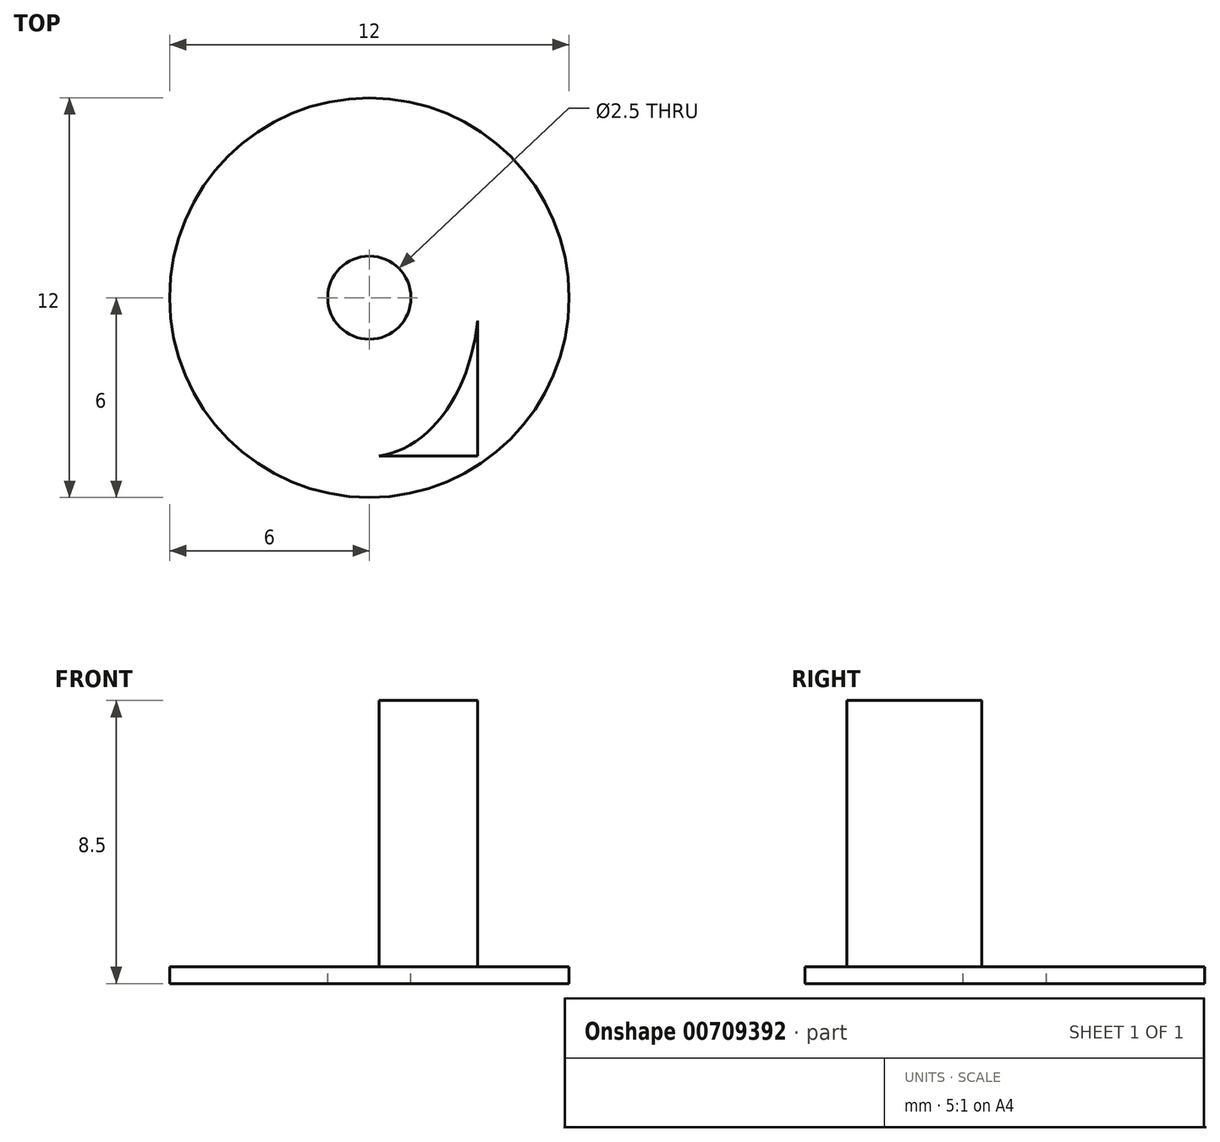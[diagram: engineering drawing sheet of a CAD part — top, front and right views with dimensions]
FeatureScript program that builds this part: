
annotation { "Feature Type Name" : "Feature", "Feature Type Description" : "" }
export const myFeature = defineFeature(function(context is Context, id is Id, definition is map)
    precondition{}
    {
        {
            var Q0;
            Q0=qCreatedBy(makeId("Top.planeOp"),FACE);
            var sketch = newSketch(context, id + "F0", { "sketchPlane" : qUnion([Q0])});
            skLineSegment(sketch, "E0.bottom", {"start": v(0, 0) * mm, "end": v(6.5, 0) * mm});
            skLineSegment(sketch, "E0.top", {"start": v(0, 9.5) * mm, "end": v(6.5, 9.5) * mm});
            skLineSegment(sketch, "E0.left", {"start": v(0, 0) * mm, "end": v(0, 9.5) * mm});
            skLineSegment(sketch, "E0.right", {"start": v(6.5, 0) * mm, "end": v(6.5, 9.5) * mm});
            skEllipse(sketch, "E1", {"center": v(3.25, 4.75) * mm, "majorRadius": 4.77 * mm, "minorRadius": 3.29 * mm, "majorAxis": v(0, -1)});
            skPoint(sketch, "E1.centerSnap0", {"position": v(0, 4.75) * mm});
            skPoint(sketch, "E1.centerSnap1", {"position": v(3.25, 9.5) * mm});
            skSolve(sketch);
        }
        {
            var Q0;
            {var subQ0=sQuery(id+"F0.wireOp",EDGE,"E1");var subQ7=sQuery(id+"F0.wireOp",EDGE,"E0.bottom");var subQ8=makeQuery(id+"F0.imprint","INTERSECT",VERTEX,{"disambiguationData":[OD(0.0)],"derivedFrom":[subQ7,subQ0]});Q0=makeQuery(id+"F0.imprint","IMPRINT",FACE,{"disambiguationData":[TD([[makeQuery(id+"F0.imprint","IMPRINT",EDGE,{"disambiguationData":[TD([[subQ8,-1.0]])],"derivedFrom":subQ7}),1.0]])]});}
            extrude(context, id + "F1", {"entities" : qUnion([Q0]), "depth" : 8 * mm, "offsetDistance" : 25 * mm});
        }
        {
            var Q0;
            Q0=makeQuery(id+"F1.opExtrude","CAP_FACE",FACE,{"disambiguationData":[OSD([sQuery(id+"F0.wireOp",EDGE,"E0.bottom"),sQuery(id+"F0.wireOp",EDGE,"E0.top"),sQuery(id+"F0.wireOp",EDGE,"E0.left"),sQuery(id+"F0.wireOp",EDGE,"E0.right"),sQuery(id+"F0.wireOp",EDGE,"E1")])],"isStart":true});
            var sketch = newSketch(context, id + "F2", { "sketchPlane" : qUnion([Q0])});
            skCircle(sketch, "E2", {"center": v(3.25, -4.75) * mm, "radius": 6 * mm});
            skCircle(sketch, "E3", {"center": v(3.25, -4.75) * mm, "radius": 1.25 * mm});
            skSolve(sketch);
        }
        {
            var Q0;
            Q0=makeQuery(id+"F2.imprint","IMPRINT",FACE,{"disambiguationData":[TD([[makeQuery(id+"F2.imprint","IMPRINT",EDGE,{"derivedFrom":sQuery(id+"F2.wireOp",EDGE,"E2")}),1.0]])]});
            var Q1;
            {var subQ3=sQuery(id+"F0.wireOp",EDGE,"E0.bottom");Q1=makeQuery(id+"F2.imprint","IMPRINT",FACE,{"disambiguationData":[TD([[makeQuery(id+"F2.imprint","IMPRINT",EDGE,{"derivedFrom":makeQuery(id+"F1.opExtrude","CAP_EDGE",EDGE,{"disambiguationData":[OSD([subQ3])],"isStart":true})}),-1.0]])]});}
            extrude(context, id + "F3", {"entities" : qUnion([Q0, Q1]), "depth" : .5 * mm, "offsetDistance" : 25 * mm});
        }
        {
            var Q0;
            Q0=makeQuery(id+"F2.imprint","IMPRINT",FACE,{"disambiguationData":[TD([[makeQuery(id+"F2.imprint","IMPRINT",EDGE,{"derivedFrom":sQuery(id+"F2.wireOp",EDGE,"E3")}),1.0]])]});
            extrude(context, id + "F4", {"entities" : qUnion([Q0]), "operationType" : NewBodyOperationType.REMOVE, "oppositeDirection" : true, "depth" : 7 * mm, "offsetDistance" : 25 * mm});
        }
    });
